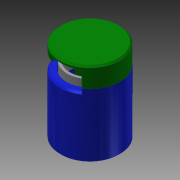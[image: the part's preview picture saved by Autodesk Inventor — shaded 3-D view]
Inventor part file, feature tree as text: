
AUTODESK INVENTOR PART (.ipt)
format: ipt  version: 2014 (Build 180170000, 170)  size: 357,376 bytes
history: native  units: mm
features: extrude x14, sketch x12, projected_geometry x11, plane x4, other x3, chamfer x2, fillet x1, boolean_combine x1, split x1
ambient origin geometry x8: Origin, YZ Plane, XZ Plane, XY Plane, X Axis, Y Axis, Z Axis, Center Point
bodies: Solid1 (feature_tree), Solid2 (feature_tree), Solid3 (feature_tree)
feature tree (49):
  extrude  "Extrusion1"  Depth=25.0mm TaperAngle=0.0deg
  plane  "Work Plane1"
  extrude  "Extrusion2"  Depth=0.4mm
  extrude  "Extrusion3"  Depth=36.0mm
  extrude  "Extrusion6"  Depth=123.83mm
  fillet  "Fillet1"  Radius=123.83mm
  plane  "Work Plane2"
  extrude  "Extrusion4"  Depth=7.35mm
  extrude  "Extrusion5"  TaperAngle=0.0deg  [1 undecoded]
  boolean_combine  "Combine1"
  sketch  "Sketch7"  dims[d14=6.0mm d15=1.8mm]
  extrude  "Extrusion7"  Depth=6.0mm
  extrude  "Extrusion8"  TaperAngle=0.0deg  [1 undecoded]
  sketch  "Sketch8"  dims[d16=8.1mm d17=0.0mm]
  extrude  "Extrusion9"  Depth=4.0mm
  plane  "Work Plane3"
  plane  "Work Plane4"
  split  "Split2"
  sketch  "Sketch11"  dims[d21=2.7mm d22=9.3mm]
  extrude  "Extrusion10"  Depth=2.7mm
  extrude  "Extrusion11"  TaperAngle=0.0deg  [1 undecoded]
  chamfer  "Chamfer1"  Distance=4.0mm
  chamfer  "Chamfer2"  Distance=4.0mm
  sketch  "Sketch12"  dims[d23=1.08mm d24=0.0mm]
  extrude  "Extrusion12"  Depth=11.0mm
  extrude  "Extrusion13"  Depth=3.0mm
  extrude  "Extrusion14"  Depth=13.0mm TaperAngle=0.0deg
  sketch  "Sketch1"  dims[d0=27.0mm d1=25.0mm d2=0.0mm]
  sketch  "Sketch2"  dims[d3=11.0mm d4=0.4mm]
  projected_geometry  "Projected Loop1"
  sketch  "Sketch3"  dims[d5=4.0mm d6=36.0mm]
  sketch  "Sketch4"  dims[d7=0.0mm d8=58.57mm d9=123.83mm]
  projected_geometry  "Projected Loop2"
  sketch  "Sketch5"  dims[d10=9.28mm d11=7.35mm]
  sketch  "Sketch6"  dims[d12=8.1mm d13=0.0mm]
  projected_geometry  "Projected Loop3"
  projected_geometry  "Projected Loop4"
  projected_geometry  "Projected Loop5"
  projected_geometry  "Projected Loop6"
  projected_geometry  "Projected Loop7"
  sketch  "Sketch9"  dims[d18=4.0mm d19=0.0mm d20=10.5mm]
  projected_geometry  "Projected Loop8"
  projected_geometry  "Projected Loop9"
  sketch  "Sketch13"  dims[d25=0.5mm d26=4.0mm d27=0.0mm d28=4.0mm d29=0.0mm d30=22.0mm d31=3.0mm d32=13.0mm d33=0.0mm d34=3.0mm d35=0.0mm d38=0.0mm d39=1.5mm d40=0.5mm d41=2.1mm d42=0.0mm d43=2.0mm d44=0.0mm d45=1.0mm d46=2.0mm d47=45.0deg d48=1.0mm d49=2.0mm d50=45.0deg d51=3.0mm d52=30.0mm d53=0.4mm d54=3.0mm d55=0.0mm d56=3.0mm d57=0.0mm d58=0.4mm d59=1.5mm d60=11.0mm d61=0.0mm]
  projected_geometry  "Projected Loop11"
  other  "focus_offset_ring"
  other  "adapter_rear"
  other  "adapter_front"
  projected_geometry  "Project Cut Edges1"
note: 3 required parameter values undecoded (feature->parameter linkage not recoverable at this tier; creation-order binding heuristic only, values carry confidence <= 0.55)
